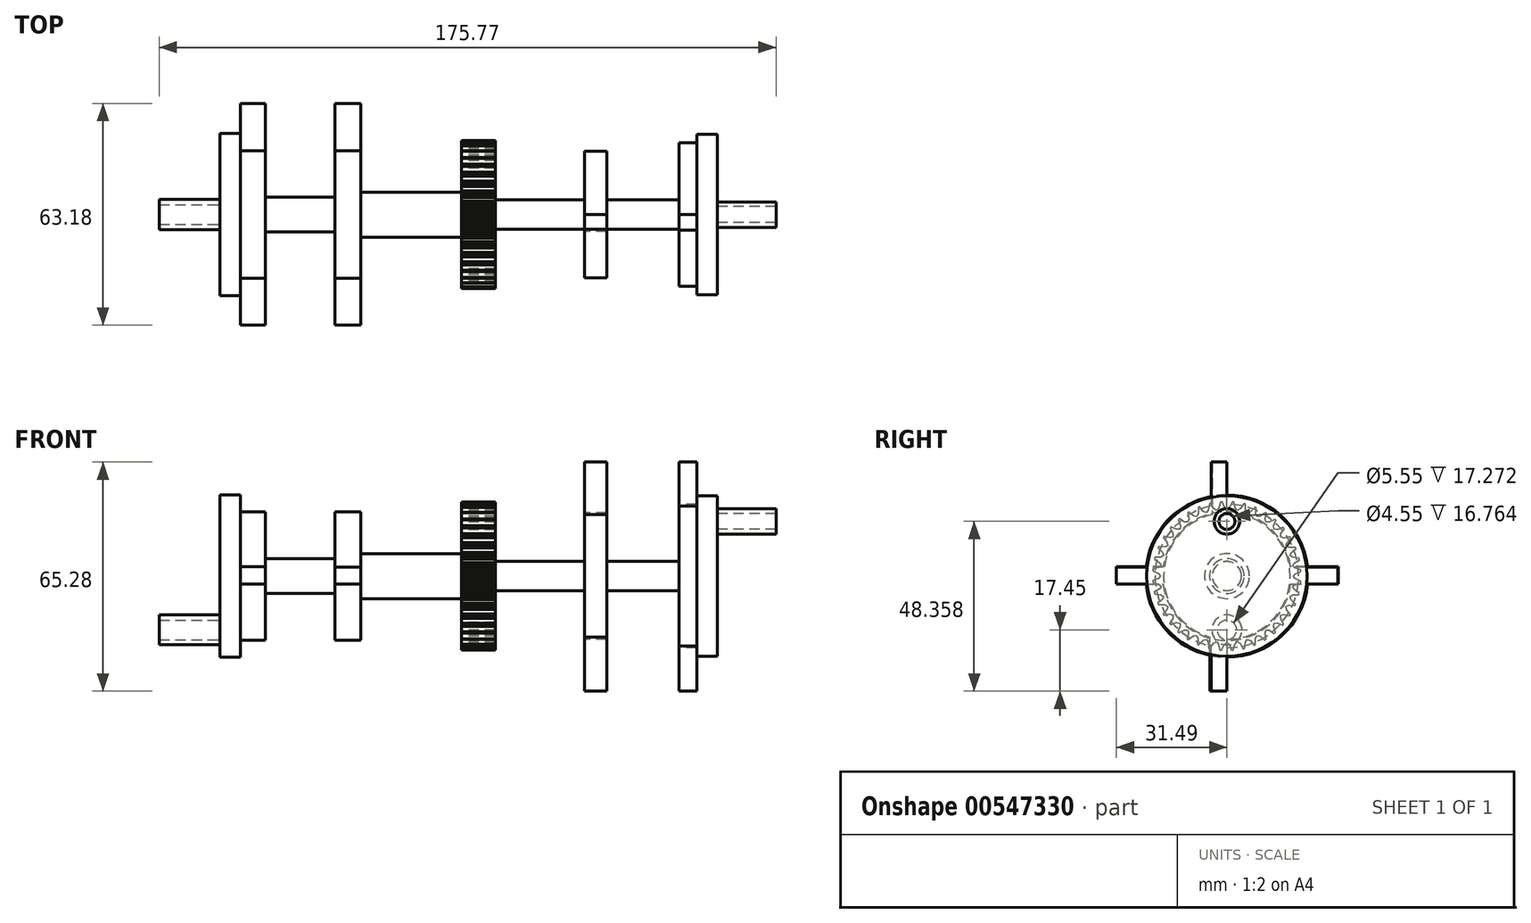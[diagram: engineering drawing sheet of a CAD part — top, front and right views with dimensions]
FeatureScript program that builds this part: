
annotation { "Feature Type Name" : "Feature", "Feature Type Description" : "" }
export const myFeature = defineFeature(function(context is Context, id is Id, definition is map)
    precondition{}
    {
        {
            var Q0;
            Q0=qCreatedBy(makeId("Right.planeOp"),FACE);
            var sketch = newSketch(context, id + "F0", { "sketchPlane" : qUnion([Q0])});
            skCircle(sketch, "E0", {"center": v(0, 0) * mm, "radius": 20.47 * mm});
            skLineSegment(sketch, "E1", {"start": v(0, -20.47) * mm, "end": v(0, -32.87) * mm});
            skLineSegment(sketch, "E2", {"start": v(0, -32.87) * mm, "end": v(-4.43, -32.81) * mm});
            skLineSegment(sketch, "E3", {"start": v(-4.43, -32.81) * mm, "end": v(-4.43, -19.99) * mm});
            skLineSegment(sketch, "E4.MirrorCS", {"start": v(0, 32.87) * mm, "end": v(-4.43, 32.81) * mm});
            skLineSegment(sketch, "E5.MirrorCS", {"start": v(-4.43, 32.81) * mm, "end": v(-4.43, 19.99) * mm});
            skLineSegment(sketch, "E6.MirrorCS", {"start": v(0, 20.47) * mm, "end": v(0, 32.87) * mm});
            skSolve(sketch);
        }
        {
            var Q0;
            {var subQ0=sQuery(id+"F0.wireOp",EDGE,"E0");var subQ1=makeQuery(id+"F0.imprint","INTERSECT",VERTEX,{"derivedFrom":[subQ0,sQuery(id+"F0.wireOp",EDGE,"ybv6XF9e-yQJ6-GcxN-1k9M-g7d4zqfCFwmI")]});Q0=makeQuery(id+"F0.imprint","IMPRINT",FACE,{"disambiguationData":[TD([[makeQuery(id+"F0.imprint","IMPRINT",EDGE,{"disambiguationData":[TD([[subQ1,1.0]])],"derivedFrom":subQ0}),1.0]])]});}
            var Q1;
            {var subQ0=sQuery(id+"F0.wireOp",EDGE,"ybv6XF9e-yQJ6-GcxN-1k9M-g7d4zqfCFwmI");Q1=makeQuery(id+"F0.imprint","IMPRINT",FACE,{"disambiguationData":[TD([[makeQuery(id+"F0.imprint","IMPRINT",EDGE,{"derivedFrom":subQ0}),-1.0]])]});}
            var Q2;
            {var subQ0=sQuery(id+"F0.wireOp",EDGE,"E1");Q2=makeQuery(id+"F0.imprint","IMPRINT",FACE,{"disambiguationData":[TD([[makeQuery(id+"F0.imprint","IMPRINT",EDGE,{"derivedFrom":subQ0}),-1.0]])]});}
            var Q3;
            Q3=makeQuery(id+"F0.imprint","IMPRINT",FACE,{"disambiguationData":[TD([[makeQuery(id+"F0.imprint","IMPRINT",EDGE,{"derivedFrom":sQuery(id+"F0.wireOp",EDGE,"E4.MirrorCS")}),1.0]])]});
            extrude(context, id + "F1", {"entities" : qUnion([Q0, Q1, Q2, Q3]), "depth" : 5.08 * mm, "offsetDistance" : 25.4 * mm});
        }
        {
            var Q0;
            Q0=makeQuery(id+"F1.opExtrude","CAP_FACE",FACE,{"disambiguationData":[OSD([sQuery(id+"F0.wireOp",EDGE,"E0"),sQuery(id+"F0.wireOp",EDGE,"ybv6XF9e-yQJ6-GcxN-1k9M-g7d4zqfCFwmI"),sQuery(id+"F0.wireOp",EDGE,"egRvkigp-FsvL-QF5D-I4YD-MoUuUeyJkvTS"),sQuery(id+"F0.wireOp",EDGE,"ktJIH1Pw-zPiB-Zv6z-c4OE-IvtrcdQjdgDW"),sQuery(id+"F0.wireOp",EDGE,"E1"),sQuery(id+"F0.wireOp",EDGE,"E2"),sQuery(id+"F0.wireOp",EDGE,"E3")])],"isStart":false});
            var sketch = newSketch(context, id + "F2", { "sketchPlane" : qUnion([Q0])});
            skCircle(sketch, "E7", {"center": v(0, 0) * mm, "radius": 22.86 * mm});
            skSolve(sketch);
        }
        {
            var Q0;
            {var subQ1=sQuery(id+"F0.wireOp",EDGE,"ybv6XF9e-yQJ6-GcxN-1k9M-g7d4zqfCFwmI");var subQ7=sQuery(id+"F0.wireOp",EDGE,"E0");var subQ8=makeQuery(id+"F1.opExtrude","CAP_EDGE",EDGE,{"disambiguationData":[OSD([subQ7]),TDD([makeQuery(id+"F0.imprint","IMPRINT",EDGE,{"disambiguationData":[TD([[makeQuery(id+"F0.imprint","INTERSECT",VERTEX,{"derivedFrom":[subQ7,subQ1]}),-1.0]])],"derivedFrom":subQ7})])],"isStart":false});Q0=makeQuery(id+"F2.imprint","IMPRINT",FACE,{"disambiguationData":[TD([[makeQuery(id+"F2.imprint","IMPRINT",EDGE,{"derivedFrom":subQ8}),-1.0]])]});}
            var Q1;
            {var subQ0=sQuery(id+"F0.wireOp",EDGE,"ybv6XF9e-yQJ6-GcxN-1k9M-g7d4zqfCFwmI");var subQ1=sQuery(id+"F0.wireOp",EDGE,"E0");var subQ3=makeQuery(id+"F1.opExtrude","CAP_EDGE",EDGE,{"disambiguationData":[OSD([subQ1]),TDD([makeQuery(id+"F0.imprint","IMPRINT",EDGE,{"disambiguationData":[TD([[makeQuery(id+"F0.imprint","INTERSECT",VERTEX,{"derivedFrom":[subQ1,subQ0]}),-1.0]])],"derivedFrom":subQ1})])],"isStart":false});Q1=makeQuery(id+"F2.imprint","IMPRINT",FACE,{"disambiguationData":[TD([[makeQuery(id+"F2.imprint","IMPRINT",EDGE,{"derivedFrom":subQ3}),1.0]])]});}
            var Q2;
            {var subQ1=sQuery(id+"F0.wireOp",EDGE,"ktJIH1Pw-zPiB-Zv6z-c4OE-IvtrcdQjdgDW");var subQ7=sQuery(id+"F0.wireOp",EDGE,"E0");var subQ8=makeQuery(id+"F1.opExtrude","CAP_EDGE",EDGE,{"disambiguationData":[OSD([subQ7]),TDD([makeQuery(id+"F0.imprint","IMPRINT",EDGE,{"disambiguationData":[TD([[makeQuery(id+"F0.imprint","INTERSECT",VERTEX,{"derivedFrom":[subQ7,subQ1]}),1.0]])],"derivedFrom":subQ7})])],"isStart":false});Q2=makeQuery(id+"F2.imprint","IMPRINT",FACE,{"disambiguationData":[TD([[makeQuery(id+"F2.imprint","IMPRINT",EDGE,{"derivedFrom":subQ8}),-1.0]])]});}
            extrude(context, id + "F3", {"entities" : qUnion([Q0, Q1, Q2]), "operationType" : NewBodyOperationType.ADD, "depth" : 5.84 * mm, "offsetDistance" : 25.4 * mm});
        }
        {
            var Q0;
            Q0=makeQuery(id+"F3.opExtrude","CAP_FACE",FACE,{"disambiguationData":[OSD([sQuery(id+"F2.wireOp",EDGE,"E7")])],"isStart":false});
            var sketch = newSketch(context, id + "F4", { "sketchPlane" : qUnion([Q0])});
            skSolve(sketch);
        }
        {
            var Q0;
            Q0=makeQuery(id+"F1.opExtrude","CAP_FACE",FACE,{"disambiguationData":[OSD([sQuery(id+"F0.wireOp",EDGE,"E0"),sQuery(id+"F0.wireOp",EDGE,"ybv6XF9e-yQJ6-GcxN-1k9M-g7d4zqfCFwmI"),sQuery(id+"F0.wireOp",EDGE,"egRvkigp-FsvL-QF5D-I4YD-MoUuUeyJkvTS"),sQuery(id+"F0.wireOp",EDGE,"ktJIH1Pw-zPiB-Zv6z-c4OE-IvtrcdQjdgDW"),sQuery(id+"F0.wireOp",EDGE,"E1"),sQuery(id+"F0.wireOp",EDGE,"E2"),sQuery(id+"F0.wireOp",EDGE,"E3")])],"isStart":true});
            var sketch = newSketch(context, id + "F5", { "sketchPlane" : qUnion([Q0])});
            skCircle(sketch, "E8", {"center": v(0, 0) * mm, "radius": 4.15 * mm});
            skSolve(sketch);
        }
        {
            var Q0;
            Q0=makeQuery(id+"F5.imprint","IMPRINT",FACE,{"disambiguationData":[TD([[makeQuery(id+"F5.imprint","IMPRINT",EDGE,{"derivedFrom":sQuery(id+"F5.wireOp",EDGE,"E8")}),1.0]])]});
            extrude(context, id + "F6", {"entities" : qUnion([Q0]), "operationType" : NewBodyOperationType.ADD, "depth" : 26.92 * mm, "offsetDistance" : 25.4 * mm});
        }
        {
            var Q0;
            Q0=makeQuery(id+"F6.opExtrude","CAP_FACE",FACE,{"disambiguationData":[OSD([sQuery(id+"F5.wireOp",EDGE,"E8")])],"isStart":false});
            var sketch = newSketch(context, id + "F7", { "sketchPlane" : qUnion([Q0])});
            skCircle(sketch, "E9", {"center": v(0, 0) * mm, "radius": 18.03 * mm});
            skLineSegment(sketch, "E10", {"start": v(0, 18.03) * mm, "end": v(0, 39.42) * mm});
            skLineSegment(sketch, "E11", {"start": v(0, 39.42) * mm, "end": v(4.15, 42.4) * mm});
            skLineSegment(sketch, "E12", {"start": v(4.15, 42.4) * mm, "end": v(4.15, 17.54) * mm});
            skLineSegment(sketch, "E13", {"start": v(0, -18.03) * mm, "end": v(0, -39.5) * mm});
            skLineSegment(sketch, "E14", {"start": v(0, -39.5) * mm, "end": v(4.79, -37.15) * mm});
            skLineSegment(sketch, "E15", {"start": v(4.79, -37.15) * mm, "end": v(4.79, -17.38) * mm});
            skSolve(sketch);
        }
        {
            var Q0;
            Q0=makeQuery(id+"F7.imprint","IMPRINT",FACE,{"disambiguationData":[TD([[makeQuery(id+"F7.imprint","IMPRINT",EDGE,{"derivedFrom":makeQuery(id+"F6.opExtrude","CAP_EDGE",EDGE,{"disambiguationData":[OSD([sQuery(id+"F5.wireOp",EDGE,"E8")])],"isStart":false})}),-1.0]])]});
            var Q1;
            {var subQ0=sQuery(id+"F7.wireOp",EDGE,"E10");Q1=makeQuery(id+"F7.imprint","IMPRINT",FACE,{"disambiguationData":[TD([[makeQuery(id+"F7.imprint","IMPRINT",EDGE,{"derivedFrom":subQ0}),-1.0]])]});}
            var Q2;
            {var subQ0=sQuery(id+"F7.wireOp",EDGE,"E13");Q2=makeQuery(id+"F7.imprint","IMPRINT",FACE,{"disambiguationData":[TD([[makeQuery(id+"F7.imprint","IMPRINT",EDGE,{"derivedFrom":subQ0}),1.0]])]});}
            extrude(context, id + "F8", {"entities" : qUnion([Q0, Q1, Q2]), "operationType" : NewBodyOperationType.ADD, "oppositeDirection" : true, "depth" : 6.35 * mm, "offsetDistance" : 25.4 * mm});
        }
        {
            var Q0;
            {var subQ0=sQuery(id+"F5.wireOp",EDGE,"E8");Q0=makeQuery(id+"F8.boolean.opBoolean","MERGE",FACE,{"derivedFrom":[makeQuery(id+"F6.opExtrude","CAP_FACE",FACE,{"disambiguationData":[OSD([subQ0])],"isStart":false}),makeQuery(id+"F8.opExtrude","CAP_FACE",FACE,{"disambiguationData":[OSD([subQ0,sQuery(id+"F7.wireOp",EDGE,"E9"),sQuery(id+"F7.wireOp",EDGE,"E10"),sQuery(id+"F7.wireOp",EDGE,"E11"),sQuery(id+"F7.wireOp",EDGE,"E12"),sQuery(id+"F7.wireOp",EDGE,"E13"),sQuery(id+"F7.wireOp",EDGE,"E14"),sQuery(id+"F7.wireOp",EDGE,"E15")])],"isStart":true})]});}
            var sketch = newSketch(context, id + "F9", { "sketchPlane" : qUnion([Q0])});
            skCircle(sketch, "E16", {"center": v(0, 0) * mm, "radius": 4.15 * mm});
            skSolve(sketch);
        }
        {
            var Q0;
            Q0=makeQuery(id+"F9.imprint","IMPRINT",FACE,{"disambiguationData":[TD([[makeQuery(id+"F9.imprint","IMPRINT",EDGE,{"derivedFrom":sQuery(id+"F9.wireOp",EDGE,"E16")}),1.0]])]});
            extrude(context, id + "F10", {"entities" : qUnion([Q0]), "operationType" : NewBodyOperationType.ADD, "depth" : 25.4 * mm, "offsetDistance" : 25.4 * mm});
        }
        {
            var Q0;
            Q0=qCreatedBy(makeId("Front.planeOp"),FACE);
            var sketch = newSketch(context, id + "F11", { "sketchPlane" : qUnion([Q0])});
            skLineSegment(sketch, "E17.bottom", {"start": v(-72.04, 32.49) * mm, "end": v(12.18, 32.49) * mm});
            skLineSegment(sketch, "E17.top", {"start": v(-72.04, 43.92) * mm, "end": v(12.18, 43.92) * mm});
            skLineSegment(sketch, "E17.left", {"start": v(-72.04, 32.49) * mm, "end": v(-72.04, 43.92) * mm});
            skLineSegment(sketch, "E17.right", {"start": v(12.18, 32.49) * mm, "end": v(12.18, 43.92) * mm});
            skLineSegment(sketch, "E18.bottom", {"start": v(-70.54, -53.54) * mm, "end": v(14.29, -53.54) * mm});
            skLineSegment(sketch, "E18.top", {"start": v(-70.54, -32.79) * mm, "end": v(14.29, -32.79) * mm});
            skLineSegment(sketch, "E18.left", {"start": v(-70.54, -53.54) * mm, "end": v(-70.54, -32.79) * mm});
            skLineSegment(sketch, "E18.right", {"start": v(14.29, -53.54) * mm, "end": v(14.29, -32.79) * mm});
            skSolve(sketch);
        }
        {
            var Q0;
            Q0=makeQuery(id+"F11.imprint","IMPRINT",FACE,{"disambiguationData":[TD([[makeQuery(id+"F11.imprint","IMPRINT",EDGE,{"derivedFrom":sQuery(id+"F11.wireOp",EDGE,"E17.bottom")}),1.0]])]});
            var Q1;
            Q1=makeQuery(id+"F11.imprint","IMPRINT",FACE,{"disambiguationData":[TD([[makeQuery(id+"F11.imprint","IMPRINT",EDGE,{"derivedFrom":sQuery(id+"F11.wireOp",EDGE,"E18.bottom")}),1.0]])]});
            extrude(context, id + "F12", {"entities" : qUnion([Q0, Q1]), "operationType" : NewBodyOperationType.REMOVE, "depth" : 13.2 * mm, "offsetDistance" : 25.4 * mm});
        }
        {
            var Q0;
            Q0=makeQuery(id+"F10.opExtrude","CAP_FACE",FACE,{"disambiguationData":[OSD([sQuery(id+"F9.wireOp",EDGE,"E16")])],"isStart":false});
            var sketch = newSketch(context, id + "F13", { "sketchPlane" : qUnion([Q0])});
            skCircle(sketch, "E19", {"center": v(0, 0) * mm, "radius": 21.17 * mm});
            skSolve(sketch);
        }
        {
            var Q0;
            Q0=makeQuery(id+"F13.imprint","IMPRINT",FACE,{"disambiguationData":[TD([[makeQuery(id+"F13.imprint","IMPRINT",EDGE,{"derivedFrom":sQuery(id+"F13.wireOp",EDGE,"E19")}),1.0]])]});
            var Q1;
            Q1=makeQuery(id+"F13.imprint","IMPRINT",FACE,{"disambiguationData":[TD([[makeQuery(id+"F13.imprint","IMPRINT",EDGE,{"derivedFrom":makeQuery(id+"F10.opExtrude","CAP_EDGE",EDGE,{"disambiguationData":[OSD([sQuery(id+"F9.wireOp",EDGE,"E16")])],"isStart":false})}),1.0]])]});
            var Q2;
            Q2=sQuery(id+"F13.wireOp",EDGE,"E19");
            extrude(context, id + "F14", {"entities" : qUnion([Q0, Q1]), "operationType" : NewBodyOperationType.ADD, "surfaceEntities" : qUnion([Q2]), "depth" : 9.65 * mm, "offsetDistance" : 25.4 * mm});
        }
        {
            var Q0;
            Q0=makeQuery(id+"F14.opExtrude","CAP_FACE",FACE,{"disambiguationData":[OSD([sQuery(id+"F13.wireOp",EDGE,"E19")])],"isStart":false});
            var sketch = newSketch(context, id + "F15", { "sketchPlane" : qUnion([Q0])});
            skLineSegment(sketch, "E20", {"start": v(-1.58, 21.1) * mm, "end": v(-0.78, 19.54) * mm});
            skLineSegment(sketch, "E21", {"start": v(-0.78, 19.54) * mm, "end": v(0, 18.95) * mm});
            skLineSegment(sketch, "E22", {"start": v(0, 18.95) * mm, "end": v(0.7, 19.54) * mm});
            skLineSegment(sketch, "E23", {"start": v(0.7, 19.54) * mm, "end": v(1.31, 21.12) * mm});
            skLineSegment(sketch, "E24", {"start": v(1.31, 21.12) * mm, "end": v(0.76, 21.54) * mm});
            skLineSegment(sketch, "E25", {"start": v(0.76, 21.54) * mm, "end": v(-0.92, 21.54) * mm});
            skLineSegment(sketch, "E26", {"start": v(-0.92, 21.54) * mm, "end": v(-1.58, 21.1) * mm});
            skSolve(sketch);
        }
        {
            var Q0;
            {var subQ1=sQuery(id+"F15.wireOp",EDGE,"E20");Q0=makeQuery(id+"F15.imprint","IMPRINT",FACE,{"disambiguationData":[TD([[makeQuery(id+"F15.imprint","IMPRINT",EDGE,{"derivedFrom":subQ1}),1.0]])]});}
            extrude(context, id + "F16", {"entities" : qUnion([Q0]), "operationType" : NewBodyOperationType.REMOVE, "oppositeDirection" : true, "depth" : 25.4 * mm, "offsetDistance" : 25.4 * mm});
        }
        {
            var Q0;
            Q0=makeQuery(id+"F16.boolean.opBoolean","COPY",FACE,{"derivedFrom":makeQuery(id+"F16.opExtrude","SWEPT_FACE",FACE,{"disambiguationData":[OSD([sQuery(id+"F15.wireOp",EDGE,"E20")])]})});
            var Q1;
            Q1=makeQuery(id+"F16.boolean.opBoolean","COPY",FACE,{"derivedFrom":makeQuery(id+"F16.opExtrude","SWEPT_FACE",FACE,{"disambiguationData":[OSD([sQuery(id+"F15.wireOp",EDGE,"E22")])]})});
            var Q2;
            Q2=makeQuery(id+"F16.boolean.opBoolean","COPY",FACE,{"derivedFrom":makeQuery(id+"F16.opExtrude","SWEPT_FACE",FACE,{"disambiguationData":[OSD([sQuery(id+"F15.wireOp",EDGE,"E23")])]})});
            var Q3;
            Q3=makeQuery(id+"F16.boolean.opBoolean","COPY",FACE,{"derivedFrom":makeQuery(id+"F16.opExtrude","SWEPT_FACE",FACE,{"disambiguationData":[OSD([sQuery(id+"F15.wireOp",EDGE,"E21")])]})});
            var Q4;
            Q4=makeQuery(id+"F14.opExtrude","SWEPT_FACE",FACE,{"disambiguationData":[OSD([sQuery(id+"F13.wireOp",EDGE,"E19")])]});
            circularPattern(context, id + "F17", {"patternType" : PatternType.FACE, "faces" : qUnion([Q0, Q1, Q2, Q3]), "axis" : qUnion([Q4]), "angle" : 360 * degree, "instanceCount" : 40, "equalSpace" : true});
        }
        {
            var Q0;
            Q0=makeQuery(id+"F14.opExtrude","CAP_FACE",FACE,{"disambiguationData":[OSD([sQuery(id+"F13.wireOp",EDGE,"E19")])],"isStart":false});
            var sketch = newSketch(context, id + "F18", { "sketchPlane" : qUnion([Q0])});
            skCircle(sketch, "E27", {"center": v(0, 0) * mm, "radius": 6.41 * mm});
            skSolve(sketch);
        }
        {
            var Q0;
            Q0=makeQuery(id+"F18.imprint","IMPRINT",FACE,{"disambiguationData":[TD([[makeQuery(id+"F18.imprint","IMPRINT",EDGE,{"derivedFrom":sQuery(id+"F18.wireOp",EDGE,"E27")}),1.0]])]});
            extrude(context, id + "F19", {"entities" : qUnion([Q0]), "operationType" : NewBodyOperationType.ADD, "depth" : 28.7 * mm, "offsetDistance" : 25.4 * mm});
        }
        {
            var Q0;
            Q0=makeQuery(id+"F19.opExtrude","CAP_FACE",FACE,{"disambiguationData":[OSD([sQuery(id+"F18.wireOp",EDGE,"E27")])],"isStart":false});
            var sketch = newSketch(context, id + "F20", { "sketchPlane" : qUnion([Q0])});
            skCircle(sketch, "E28", {"center": v(0, 0) * mm, "radius": 18.33 * mm});
            skLineSegment(sketch, "E29", {"start": v(18.15, 2.6) * mm, "end": v(31.49, 2.6) * mm});
            skLineSegment(sketch, "E30", {"start": v(31.49, 2.6) * mm, "end": v(31.49, 0) * mm});
            skLineSegment(sketch, "E31", {"start": v(31.49, 0) * mm, "end": v(31.49, -2.27) * mm});
            skLineSegment(sketch, "E32", {"start": v(31.49, -2.27) * mm, "end": v(18.2, -2.27) * mm});
            skLineSegment(sketch, "E33", {"start": v(-18.2, -2.27) * mm, "end": v(-31.6, -2.27) * mm});
            skLineSegment(sketch, "E34", {"start": v(-31.6, -2.27) * mm, "end": v(-31.6, 0) * mm});
            skLineSegment(sketch, "E35", {"start": v(-31.6, 0) * mm, "end": v(-31.6, 2.6) * mm});
            skLineSegment(sketch, "E36", {"start": v(-31.6, 2.6) * mm, "end": v(-18.15, 2.6) * mm});
            skSolve(sketch);
        }
        {
            var Q0;
            Q0=makeQuery(id+"F20.imprint","IMPRINT",FACE,{"disambiguationData":[TD([[makeQuery(id+"F20.imprint","IMPRINT",EDGE,{"derivedFrom":makeQuery(id+"F19.opExtrude","CAP_EDGE",EDGE,{"disambiguationData":[OSD([sQuery(id+"F18.wireOp",EDGE,"E27")])],"isStart":false})}),1.0]])]});
            var Q1;
            Q1=makeQuery(id+"F20.imprint","IMPRINT",FACE,{"disambiguationData":[TD([[makeQuery(id+"F20.imprint","IMPRINT",EDGE,{"derivedFrom":sQuery(id+"F20.wireOp",EDGE,"E28")}),1.0]])]});
            extrude(context, id + "F21", {"entities" : qUnion([Q0, Q1]), "operationType" : NewBodyOperationType.ADD, "depth" : 6.6 * mm, "offsetDistance" : 25.4 * mm});
        }
        {
            var Q0;
            Q0 = qSketchRegion(id + "F20", true);
            extrude(context, id + "F22", {"entities" : qUnion([Q0]), "operationType" : NewBodyOperationType.ADD, "depth" : 7.37 * mm, "offsetDistance" : 25.4 * mm});
        }
        {
            var Q0;
            Q0=makeQuery(id+"F22.opExtrude","CAP_FACE",FACE,{"disambiguationData":[OSD([sQuery(id+"F20.wireOp",EDGE,"E28"),sQuery(id+"F20.wireOp",EDGE,"E29"),sQuery(id+"F20.wireOp",EDGE,"E30"),sQuery(id+"F20.wireOp",EDGE,"E31"),sQuery(id+"F20.wireOp",EDGE,"E32"),sQuery(id+"F20.wireOp",EDGE,"E33"),sQuery(id+"F20.wireOp",EDGE,"E34"),sQuery(id+"F20.wireOp",EDGE,"E35"),sQuery(id+"F20.wireOp",EDGE,"E36")])],"isStart":false});
            var sketch = newSketch(context, id + "F23", { "sketchPlane" : qUnion([Q0])});
            skCircle(sketch, "E37", {"center": v(0, 0) * mm, "radius": 4.95 * mm});
            skSolve(sketch);
        }
        {
            var Q0;
            Q0=makeQuery(id+"F23.imprint","IMPRINT",FACE,{"disambiguationData":[TD([[makeQuery(id+"F23.imprint","IMPRINT",EDGE,{"derivedFrom":sQuery(id+"F23.wireOp",EDGE,"E37")}),1.0]])]});
            extrude(context, id + "F24", {"entities" : qUnion([Q0]), "operationType" : NewBodyOperationType.ADD, "depth" : 19.8 * mm, "offsetDistance" : 25.4 * mm});
        }
        {
            var Q0;
            Q0=makeQuery(id+"F24.opExtrude","CAP_FACE",FACE,{"disambiguationData":[OSD([sQuery(id+"F23.wireOp",EDGE,"E37")])],"isStart":false});
            var sketch = newSketch(context, id + "F25", { "sketchPlane" : qUnion([Q0])});
            skCircle(sketch, "E38", {"center": v(0, 0) * mm, "radius": 18.33 * mm});
            skLineSegment(sketch, "E39", {"start": v(-18.19, -2.25) * mm, "end": v(-31.7, -2.25) * mm});
            skLineSegment(sketch, "E40", {"start": v(-31.7, -2.25) * mm, "end": v(-31.7, 2.63) * mm});
            skLineSegment(sketch, "E41", {"start": v(-31.7, 2.63) * mm, "end": v(-18.14, 2.63) * mm});
            skLineSegment(sketch, "E42", {"start": v(18.13, 2.64) * mm, "end": v(31.48, 2.64) * mm});
            skLineSegment(sketch, "E43", {"start": v(31.48, 2.64) * mm, "end": v(31.48, -2.26) * mm});
            skLineSegment(sketch, "E44", {"start": v(31.48, -2.26) * mm, "end": v(18.19, -2.26) * mm});
            skSolve(sketch);
        }
        {
            var Q0;
            Q0=makeQuery(id+"F25.imprint","IMPRINT",FACE,{"disambiguationData":[TD([[makeQuery(id+"F25.imprint","IMPRINT",EDGE,{"derivedFrom":makeQuery(id+"F24.opExtrude","CAP_EDGE",EDGE,{"disambiguationData":[OSD([sQuery(id+"F23.wireOp",EDGE,"E37")])],"isStart":false})}),1.0]])]});
            var Q1;
            Q1=makeQuery(id+"F25.imprint","IMPRINT",FACE,{"disambiguationData":[TD([[makeQuery(id+"F25.imprint","IMPRINT",EDGE,{"derivedFrom":makeQuery(id+"F24.opExtrude","CAP_EDGE",EDGE,{"disambiguationData":[OSD([sQuery(id+"F23.wireOp",EDGE,"E37")])],"isStart":false})}),-1.0]])]});
            var Q2;
            {var subQ0=sQuery(id+"F25.wireOp",EDGE,"E39");Q2=makeQuery(id+"F25.imprint","IMPRINT",FACE,{"disambiguationData":[TD([[makeQuery(id+"F25.imprint","IMPRINT",EDGE,{"derivedFrom":subQ0}),-1.0]])]});}
            var Q3;
            {var subQ0=sQuery(id+"F25.wireOp",EDGE,"E42");Q3=makeQuery(id+"F25.imprint","IMPRINT",FACE,{"disambiguationData":[TD([[makeQuery(id+"F25.imprint","IMPRINT",EDGE,{"derivedFrom":subQ0}),-1.0]])]});}
            extrude(context, id + "F26", {"entities" : qUnion([Q0, Q1, Q2, Q3]), "operationType" : NewBodyOperationType.ADD, "depth" : 7.11 * mm, "offsetDistance" : 25.4 * mm});
        }
        {
            var Q0;
            Q0=makeQuery(id+"F26.opExtrude","CAP_FACE",FACE,{"disambiguationData":[OSD([sQuery(id+"F25.wireOp",EDGE,"E38"),sQuery(id+"F25.wireOp",EDGE,"E39"),sQuery(id+"F25.wireOp",EDGE,"E40"),sQuery(id+"F25.wireOp",EDGE,"E41"),sQuery(id+"F25.wireOp",EDGE,"E42"),sQuery(id+"F25.wireOp",EDGE,"E43"),sQuery(id+"F25.wireOp",EDGE,"E44")])],"isStart":false});
            var sketch = newSketch(context, id + "F27", { "sketchPlane" : qUnion([Q0])});
            skCircle(sketch, "E45", {"center": v(0, 0) * mm, "radius": 23.12 * mm});
            skSolve(sketch);
        }
        {
            var Q0;
            {var subQ1=sQuery(id+"F25.wireOp",EDGE,"E39");var subQ7=sQuery(id+"F25.wireOp",EDGE,"E38");var subQ8=makeQuery(id+"F26.opExtrude","CAP_EDGE",EDGE,{"disambiguationData":[OSD([subQ7]),TDD([makeQuery(id+"F25.imprint","IMPRINT",EDGE,{"disambiguationData":[TD([[makeQuery(id+"F25.imprint","INTERSECT",VERTEX,{"derivedFrom":[subQ7,subQ1]}),-1.0]])],"derivedFrom":subQ7})])],"isStart":false});Q0=makeQuery(id+"F27.imprint","IMPRINT",FACE,{"disambiguationData":[TD([[makeQuery(id+"F27.imprint","IMPRINT",EDGE,{"derivedFrom":subQ8}),-1.0]])]});}
            var Q1;
            {var subQ1=sQuery(id+"F25.wireOp",EDGE,"E38");var subQ4=sQuery(id+"F25.wireOp",EDGE,"E41");var subQ6=makeQuery(id+"F26.opExtrude","CAP_EDGE",EDGE,{"disambiguationData":[OSD([subQ1]),TDD([makeQuery(id+"F25.imprint","IMPRINT",EDGE,{"disambiguationData":[TD([[makeQuery(id+"F25.imprint","INTERSECT",VERTEX,{"derivedFrom":[subQ1,subQ4]}),1.0]])],"derivedFrom":subQ1})])],"isStart":false});Q1=makeQuery(id+"F27.imprint","IMPRINT",FACE,{"disambiguationData":[TD([[makeQuery(id+"F27.imprint","IMPRINT",EDGE,{"derivedFrom":subQ6}),1.0]])]});}
            var Q2;
            {var subQ1=sQuery(id+"F25.wireOp",EDGE,"E41");var subQ7=sQuery(id+"F25.wireOp",EDGE,"E38");var subQ8=makeQuery(id+"F26.opExtrude","CAP_EDGE",EDGE,{"disambiguationData":[OSD([subQ7]),TDD([makeQuery(id+"F25.imprint","IMPRINT",EDGE,{"disambiguationData":[TD([[makeQuery(id+"F25.imprint","INTERSECT",VERTEX,{"derivedFrom":[subQ7,subQ1]}),1.0]])],"derivedFrom":subQ7})])],"isStart":false});Q2=makeQuery(id+"F27.imprint","IMPRINT",FACE,{"disambiguationData":[TD([[makeQuery(id+"F27.imprint","IMPRINT",EDGE,{"derivedFrom":subQ8}),-1.0]])]});}
            extrude(context, id + "F28", {"entities" : qUnion([Q0, Q1, Q2]), "operationType" : NewBodyOperationType.ADD, "depth" : 5.84 * mm, "offsetDistance" : 25.4 * mm});
        }
        {
            var Q0;
            Q0=makeQuery(id+"F3.opExtrude","CAP_FACE",FACE,{"disambiguationData":[OSD([sQuery(id+"F2.wireOp",EDGE,"E7")])],"isStart":false});
            var sketch = newSketch(context, id + "F29", { "sketchPlane" : qUnion([Q0])});
            skCircle(sketch, "E46", {"center": v(0, 15.57) * mm, "radius": 3.64 * mm});
            skCircle(sketch, "E47", {"center": v(0, 15.57) * mm, "radius": 2.28 * mm});
            skSolve(sketch);
        }
        {
            var Q0;
            Q0=makeQuery(id+"F29.imprint","IMPRINT",FACE,{"disambiguationData":[TD([[makeQuery(id+"F29.imprint","IMPRINT",EDGE,{"derivedFrom":sQuery(id+"F29.wireOp",EDGE,"E46")}),1.0]])]});
            extrude(context, id + "F30", {"entities" : qUnion([Q0]), "operationType" : NewBodyOperationType.ADD, "depth" : 7.62 * mm, "offsetDistance" : 25.4 * mm});
        }
        {
            var Q0;
            Q0=makeQuery(id+"F28.opExtrude","CAP_FACE",FACE,{"disambiguationData":[OSD([sQuery(id+"F27.wireOp",EDGE,"E45")])],"isStart":false});
            var sketch = newSketch(context, id + "F31", { "sketchPlane" : qUnion([Q0])});
            skCircle(sketch, "E48", {"center": v(0, -15.34) * mm, "radius": 4.28 * mm});
            skCircle(sketch, "E49", {"center": v(0, -15.34) * mm, "radius": 2.77 * mm});
            skSolve(sketch);
        }
        {
            var Q0;
            Q0=makeQuery(id+"F31.imprint","IMPRINT",FACE,{"disambiguationData":[TD([[makeQuery(id+"F31.imprint","IMPRINT",EDGE,{"derivedFrom":sQuery(id+"F31.wireOp",EDGE,"E48")}),1.0]])]});
            extrude(context, id + "F32", {"entities" : qUnion([Q0]), "operationType" : NewBodyOperationType.ADD, "depth" : 4.57 * mm, "offsetDistance" : 25.4 * mm});
        }
        {
            var Q0;
            Q0=makeQuery(id+"F32.opExtrude","CAP_FACE",FACE,{"disambiguationData":[OSD([sQuery(id+"F31.wireOp",EDGE,"E48"),sQuery(id+"F31.wireOp",EDGE,"E49")])],"isStart":false});
            extrude(context, id + "F33", {"entities" : qUnion([Q0]), "operationType" : NewBodyOperationType.ADD, "depth" : 12.7 * mm, "offsetDistance" : 25.4 * mm});
        }
        {
            var Q0;
            Q0=makeQuery(id+"F30.opExtrude","CAP_FACE",FACE,{"disambiguationData":[OSD([sQuery(id+"F29.wireOp",EDGE,"E46"),sQuery(id+"F29.wireOp",EDGE,"E47")])],"isStart":false});
            extrude(context, id + "F34", {"entities" : qUnion([Q0]), "operationType" : NewBodyOperationType.ADD, "depth" : 9.14 * mm, "offsetDistance" : 25.4 * mm});
        }
    });
